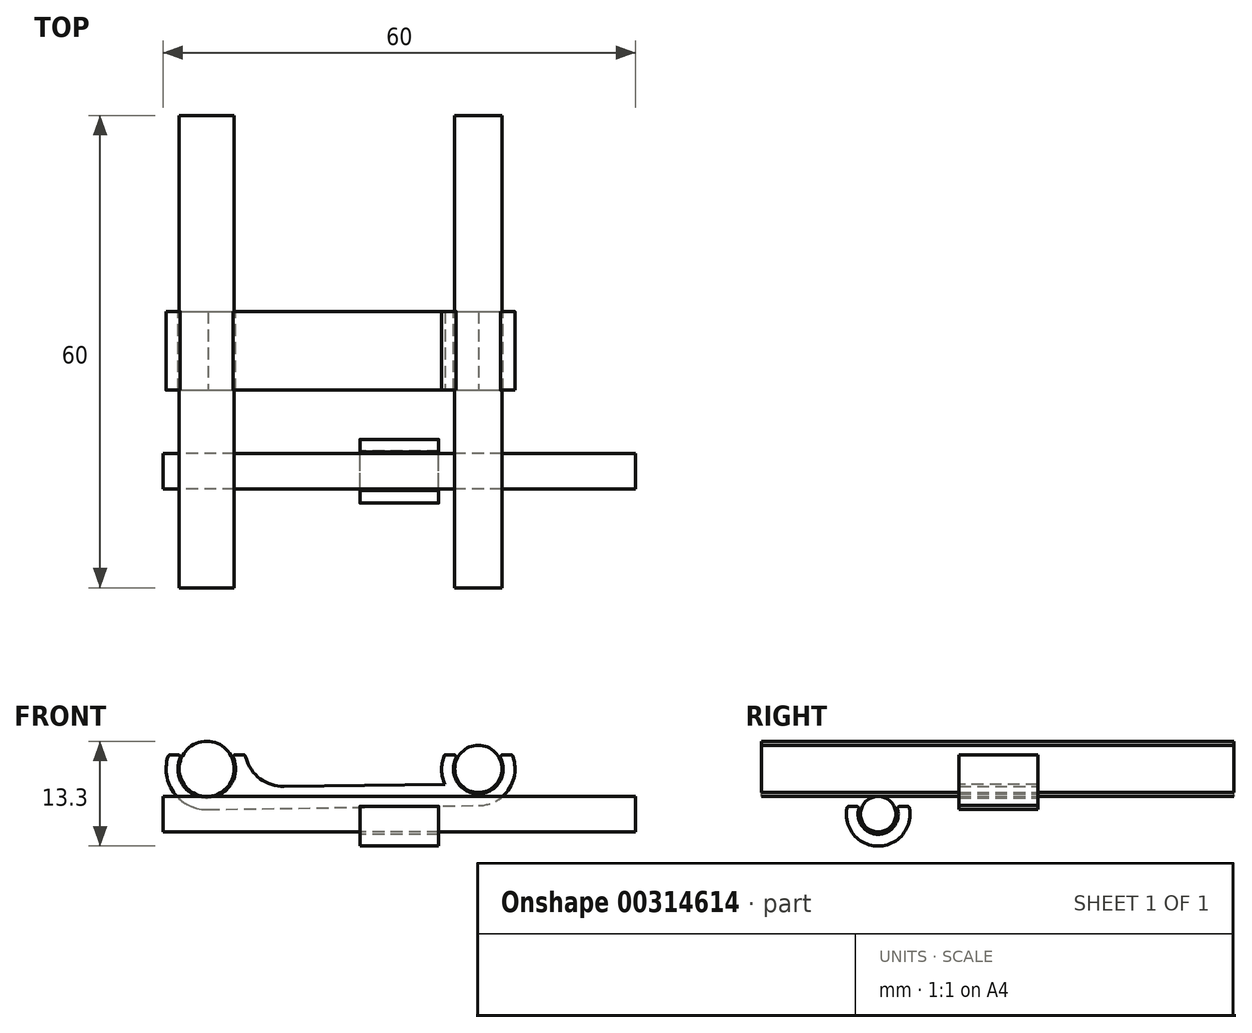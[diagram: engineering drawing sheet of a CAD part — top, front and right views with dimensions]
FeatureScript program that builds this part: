
annotation { "Feature Type Name" : "Feature", "Feature Type Description" : "" }
export const myFeature = defineFeature(function(context is Context, id is Id, definition is map)
    precondition{}
    {
        {
            var Q0;
            Q0=qCreatedBy(makeId("Front.planeOp"),FACE);
            var sketch = newSketch(context, id + "F0", { "sketchPlane" : qUnion([Q0])});
            skCircle(sketch, "E0", {"center": v(-24.47, 18.65) * mm, "radius": 3.5 * mm});
            skCircle(sketch, "E1", {"center": v(10.03, 18.65) * mm, "radius": 3 * mm});
            skLineSegment(sketch, "E2", {"start": v(-27.97, 18.65) * mm, "end": v(13.03, 18.65) * mm, "construction": true});
            skPoint(sketch, "E3", {"position": v(0, 18.65) * mm});
            skLineSegment(sketch, "E4", {"start": v(0, 0) * mm, "end": v(0, 43.05) * mm, "construction": true});
            skSolve(sketch);
        }
        {
            var Q0;
            Q0 = qSketchRegion(id + "F0", true);
            extrude(context, id + "F1", {"entities" : qUnion([Q0]), "depth" : 60 * mm});
        }
        {
            var Q0;
            Q0=qCreatedBy(makeId("Right.planeOp"),FACE);
            var sketch = newSketch(context, id + "F2", { "sketchPlane" : qUnion([Q0])});
            skCircle(sketch, "E5", {"center": v(-45.18, 12.9) * mm, "radius": 2.25 * mm});
            skLineSegment(sketch, "E6.0", {"start": v(-60, 15.15) * mm, "end": v(-60, 22.15) * mm, "construction": true});
            skLineSegment(sketch, "E7", {"start": v(-60, 15.15) * mm, "end": v(7.17, 15.15) * mm, "construction": true});
            skSolve(sketch);
        }
        {
            var Q0;
            Q0 = qSketchRegion(id + "F2", true);
            extrude(context, id + "F3", {"entities" : qUnion([Q0]), "endBound" : BoundingType.SYMMETRIC, "depth" : 60 * mm});
        }
        {
            var Q0;
            Q0=qCreatedBy(makeId("Right.planeOp"),FACE);
            var sketch = newSketch(context, id + "F4", { "sketchPlane" : qUnion([Q0])});
            skCircle(sketch, "E8.0", {"center": v(-45.18, 12.9) * mm, "radius": 2.25 * mm, "construction": true});
            skLineSegment(sketch, "E9", {"start": v(-45.18, 12.9) * mm, "end": v(-45.18, 13.9) * mm, "construction": true});
            skLineSegment(sketch, "E10", {"start": v(-41.25, 13.9) * mm, "end": v(-41.25, 13.9) * mm});
            skLineSegment(sketch, "E11", {"start": v(-47.52, 13.9) * mm, "end": v(-49.1, 13.9) * mm});
            skLineSegment(sketch, "E12", {"start": v(-42.83, 13.9) * mm, "end": v(-47.52, 13.9) * mm, "construction": true});
            skArc(sketch, "E13", {"start": v(-47.52, 13.9) * mm, "mid": v(-45.18, 10.35) * mm, "end": v(-42.83, 13.9) * mm});
            skArc(sketch, "E14", {"start": v(-42.83, 13.9) * mm, "mid": v(-45.18, 15.45) * mm, "end": v(-47.52, 13.9) * mm, "construction": true});
            skArc(sketch, "E15", {"start": v(-49.1, 13.9) * mm, "mid": v(-45.18, 8.85) * mm, "end": v(-41.25, 13.9) * mm});
            skArc(sketch, "E16", {"start": v(-41.25, 13.9) * mm, "mid": v(-45.18, 16.95) * mm, "end": v(-49.1, 13.9) * mm, "construction": true});
            skLineSegment(sketch, "E17", {"start": v(-41.25, 13.9) * mm, "end": v(-42.83, 13.9) * mm});
            skSolve(sketch);
        }
        {
            var Q0;
            Q0=makeQuery(id+"F4.imprint","IMPRINT",FACE,{"disambiguationData":[TD([[makeQuery(id+"F4.imprint","IMPRINT",EDGE,{"derivedFrom":sQuery(id+"F4.wireOp",EDGE,"E11")}),1.0]])]});
            extrude(context, id + "F5", {"entities" : qUnion([Q0]), "endBound" : BoundingType.SYMMETRIC, "depth" : 10 * mm});
        }
        {
            var Q0;
            Q0=makeQuery(id+"F5.opExtrude","SWEPT_EDGE",EDGE,{"disambiguationData":[OSD([sQuery(id+"F4.wireOp",EDGE,"E15"),sQuery(id+"F4.wireOp",EDGE,"E17")])]});
            var Q1;
            Q1=makeQuery(id+"F5.opExtrude","SWEPT_EDGE",EDGE,{"disambiguationData":[OSD([sQuery(id+"F4.wireOp",EDGE,"E13"),sQuery(id+"F4.wireOp",EDGE,"E17")])]});
            var Q2;
            Q2=makeQuery(id+"F5.opExtrude","SWEPT_EDGE",EDGE,{"disambiguationData":[OSD([sQuery(id+"F4.wireOp",EDGE,"E11"),sQuery(id+"F4.wireOp",EDGE,"E13")])]});
            var Q3;
            Q3=makeQuery(id+"F5.opExtrude","SWEPT_EDGE",EDGE,{"disambiguationData":[OSD([sQuery(id+"F4.wireOp",EDGE,"E11"),sQuery(id+"F4.wireOp",EDGE,"E15")])]});
            fillet(context, id + "F6", {"entities" : qUnion([Q0, Q1, Q2, Q3]), "radius" : 0.3 * mm, "tangentPropagation" : true, "allowEdgeOverflow" : false});
        }
        {
            var Q0;
            Q0=qCreatedBy(makeId("Front.planeOp"),FACE);
            cPlane(context, id + "F7", {"entities" : qUnion([Q0]), "cplaneType" : CPlaneType.OFFSET, "offset" : 29.9 * mm, "width" : 150 * mm, "height" : 150 * mm});
        }
        {
            var Q0;
            Q0=qCreatedBy(id+"F7.planeOp",FACE);
            var sketch = newSketch(context, id + "F8", { "sketchPlane" : qUnion([Q0])});
            skCircle(sketch, "E18.0", {"center": v(-24.47, 18.65) * mm, "radius": 3.5 * mm, "construction": true});
            skLineSegment(sketch, "E19", {"start": v(-26.27, 26.23) * mm, "end": v(-26.27, 23.48) * mm, "construction": true});
            skLineSegment(sketch, "E20", {"start": v(-26.27, 23.48) * mm, "end": v(-26.27, 21.83) * mm});
            skLineSegment(sketch, "E21", {"start": v(-26.27, 15.46) * mm, "end": v(-26.27, 13.8) * mm});
            skLineSegment(sketch, "E22", {"start": v(-26.27, 13.8) * mm, "end": v(-26.27, 11.64) * mm, "construction": true});
            skArc(sketch, "E23", {"start": v(-26.27, 21.83) * mm, "mid": v(-28.13, 18.65) * mm, "end": v(-26.27, 15.46) * mm, "construction": true});
            skArc(sketch, "E24", {"start": v(-26.27, 15.46) * mm, "mid": v(-20.8, 18.65) * mm, "end": v(-26.27, 21.83) * mm});
            skArc(sketch, "E25", {"start": v(-26.27, 13.8) * mm, "mid": v(-19.3, 18.65) * mm, "end": v(-26.27, 23.48) * mm});
            skArc(sketch, "E26", {"start": v(-26.27, 23.48) * mm, "mid": v(-29.63, 18.65) * mm, "end": v(-26.27, 13.8) * mm, "construction": true});
            skLineSegment(sketch, "E27", {"start": v(-26.27, 21.83) * mm, "end": v(-26.27, 15.46) * mm, "construction": true});
            skCircle(sketch, "E28.0", {"center": v(10.03, 18.65) * mm, "radius": 3 * mm, "construction": true});
            skLineSegment(sketch, "E29", {"start": v(11.83, 24.74) * mm, "end": v(11.83, 22.94) * mm, "construction": true});
            skArc(sketch, "E30", {"start": v(11.83, 22.94) * mm, "mid": v(5.37, 18.65) * mm, "end": v(11.83, 14.35) * mm});
            skArc(sketch, "E31", {"start": v(11.83, 14.35) * mm, "mid": v(14.7, 18.65) * mm, "end": v(11.83, 22.94) * mm, "construction": true});
            skLineSegment(sketch, "E32", {"start": v(11.83, 16.05) * mm, "end": v(11.83, 14.35) * mm});
            skArc(sketch, "E33", {"start": v(11.83, 16.05) * mm, "mid": v(13.2, 18.65) * mm, "end": v(11.83, 21.24) * mm, "construction": true});
            skArc(sketch, "E34", {"start": v(11.83, 21.24) * mm, "mid": v(6.87, 18.65) * mm, "end": v(11.83, 16.05) * mm});
            skLineSegment(sketch, "E35", {"start": v(11.83, 21.24) * mm, "end": v(11.83, 16.05) * mm, "construction": true});
            skLineSegment(sketch, "E36", {"start": v(11.83, 22.94) * mm, "end": v(11.83, 21.24) * mm});
            skLineSegment(sketch, "E37", {"start": v(11.83, 14.35) * mm, "end": v(11.83, 11.12) * mm, "construction": true});
            skSolve(sketch);
        }
        {
            var Q0;
            Q0=makeQuery(id+"F8.imprint","IMPRINT",FACE,{"disambiguationData":[TD([[makeQuery(id+"F8.imprint","IMPRINT",EDGE,{"derivedFrom":sQuery(id+"F8.wireOp",EDGE,"E20")}),1.0]])]});
            var Q1;
            Q1=makeQuery(id+"F8.imprint","IMPRINT",FACE,{"disambiguationData":[TD([[makeQuery(id+"F8.imprint","IMPRINT",EDGE,{"derivedFrom":sQuery(id+"F8.wireOp",EDGE,"E30")}),1.0]])]});
            extrude(context, id + "F9", {"entities" : qUnion([Q0, Q1]), "endBound" : BoundingType.SYMMETRIC, "depth" : 10 * mm});
        }
        {
            var Q0;
            Q0=makeQuery(id+"F9.opExtrude","SWEPT_BODY",BODY,{"disambiguationData":[OSD([sQuery(id+"F8.wireOp",EDGE,"E20"),sQuery(id+"F8.wireOp",EDGE,"E21"),sQuery(id+"F8.wireOp",EDGE,"E24"),sQuery(id+"F8.wireOp",EDGE,"E25")])]});
            var Q1;
            Q1=makeQuery(id+"F1.opExtrude","SWEPT_FACE",FACE,{"disambiguationData":[OSD([sQuery(id+"F0.wireOp",EDGE,"E0")])]});
            transform(context, id + "F10", {"entities" : qUnion([Q0]), "transformType" : TransformType.ROTATION, "transformAxis" : qUnion([Q1]), "angle" : 90 * degree, "makeCopy" : false});
        }
        {
            var Q0;
            Q0=makeQuery(id+"F9.opExtrude","SWEPT_BODY",BODY,{"disambiguationData":[OSD([sQuery(id+"F8.wireOp",EDGE,"E30"),sQuery(id+"F8.wireOp",EDGE,"E32"),sQuery(id+"F8.wireOp",EDGE,"E34"),sQuery(id+"F8.wireOp",EDGE,"E36")])]});
            var Q1;
            Q1=makeQuery(id+"F9.opExtrude","CAP_EDGE",EDGE,{"disambiguationData":[OSD([sQuery(id+"F8.wireOp",EDGE,"E32")])],"isStart":true});
            var Q2;
            Q2=makeQuery(id+"F9.opExtrude","CAP_VERTEX",VERTEX,{"disambiguationData":[OSD([sQuery(id+"F8.wireOp",EDGE,"E30"),sQuery(id+"F8.wireOp",EDGE,"E32")])],"isStart":true});
            var Q3;
            Q3=makeQuery(id+"F1.opExtrude","SWEPT_FACE",FACE,{"disambiguationData":[OSD([sQuery(id+"F0.wireOp",EDGE,"E1")])]});
            transform(context, id + "F11", {"entities" : qUnion([Q0]), "transformType" : TransformType.ROTATION, "transformAxis" : qUnion([Q3]), "angle" : 270 * degree, "makeCopy" : false});
        }
        {
            var Q0;
            Q0=makeQuery(id+"F9.opExtrude","CAP_FACE",FACE,{"disambiguationData":[OSD([sQuery(id+"F8.wireOp",EDGE,"E20"),sQuery(id+"F8.wireOp",EDGE,"E21"),sQuery(id+"F8.wireOp",EDGE,"E24"),sQuery(id+"F8.wireOp",EDGE,"E25")])],"isStart":false});
            var sketch = newSketch(context, id + "F12", { "sketchPlane" : qUnion([Q0])});
            skLineSegment(sketch, "E38.1.0", {"start": v(7.44, 20.45) * mm, "end": v(5.73, 20.45) * mm});
            skArc(sketch, "E38.1.1", {"start": v(5.73, 20.45) * mm, "mid": v(10.03, 13.99) * mm, "end": v(14.33, 20.45) * mm});
            skLineSegment(sketch, "E38.1.2", {"start": v(14.33, 20.45) * mm, "end": v(12.63, 20.45) * mm});
            skArc(sketch, "E38.1.3", {"start": v(12.63, 20.45) * mm, "mid": v(10.03, 15.49) * mm, "end": v(7.44, 20.45) * mm});
            skArc(sketch, "E39.0", {"start": v(-29.3, 20.45) * mm, "mid": v(-24.47, 13.49) * mm, "end": v(-19.63, 20.45) * mm});
            skLineSegment(sketch, "E40", {"start": v(-24.47, 13.49) * mm, "end": v(10.03, 13.99) * mm});
            skLineSegment(sketch, "E41", {"start": v(-19.86, 16.33) * mm, "end": v(5.8, 16.7) * mm});
            skSolve(sketch);
        }
        {
            var Q0;
            {var subQ3=sQuery(id+"F12.wireOp",EDGE,"E41");Q0=makeQuery(id+"F12.imprint","IMPRINT",FACE,{"disambiguationData":[TD([[makeQuery(id+"F12.imprint","IMPRINT",EDGE,{"derivedFrom":subQ3}),-1.0]])]});}
            extrude(context, id + "F13", {"entities" : qUnion([Q0]), "operationType" : NewBodyOperationType.ADD, "oppositeDirection" : true, "depth" : 10 * mm});
        }
        {
            var Q0;
            Q0=makeQuery(id+"F9.opExtrude","SWEPT_EDGE",EDGE,{"disambiguationData":[OSD([sQuery(id+"F8.wireOp",EDGE,"E20"),sQuery(id+"F8.wireOp",EDGE,"E25")])]});
            var Q1;
            Q1=makeQuery(id+"F9.opExtrude","SWEPT_EDGE",EDGE,{"disambiguationData":[OSD([sQuery(id+"F8.wireOp",EDGE,"E20"),sQuery(id+"F8.wireOp",EDGE,"E24")])]});
            var Q2;
            Q2=makeQuery(id+"F9.opExtrude","SWEPT_EDGE",EDGE,{"disambiguationData":[OSD([sQuery(id+"F8.wireOp",EDGE,"E21"),sQuery(id+"F8.wireOp",EDGE,"E24")])]});
            var Q3;
            Q3=makeQuery(id+"F9.opExtrude","SWEPT_EDGE",EDGE,{"disambiguationData":[OSD([sQuery(id+"F8.wireOp",EDGE,"E21"),sQuery(id+"F8.wireOp",EDGE,"E25")])]});
            var Q4;
            Q4=makeQuery(id+"F9.opExtrude","SWEPT_EDGE",EDGE,{"disambiguationData":[OSD([sQuery(id+"F8.wireOp",EDGE,"E34"),sQuery(id+"F8.wireOp",EDGE,"E36")])]});
            var Q5;
            Q5=makeQuery(id+"F9.opExtrude","SWEPT_EDGE",EDGE,{"disambiguationData":[OSD([sQuery(id+"F8.wireOp",EDGE,"E30"),sQuery(id+"F8.wireOp",EDGE,"E36")])]});
            var Q6;
            Q6=makeQuery(id+"F9.opExtrude","SWEPT_EDGE",EDGE,{"disambiguationData":[OSD([sQuery(id+"F8.wireOp",EDGE,"E30"),sQuery(id+"F8.wireOp",EDGE,"E32")])]});
            var Q7;
            Q7=makeQuery(id+"F9.opExtrude","SWEPT_EDGE",EDGE,{"disambiguationData":[OSD([sQuery(id+"F8.wireOp",EDGE,"E32"),sQuery(id+"F8.wireOp",EDGE,"E34")])]});
            fillet(context, id + "F14", {"entities" : qUnion([Q0, Q1, Q2, Q3, Q4, Q5, Q6, Q7]), "radius" : 0.3 * mm, "tangentPropagation" : true, "allowEdgeOverflow" : false});
        }
        {
            var Q0;
            Q0=makeQuery(id+"F13.opExtrude","SWEPT_EDGE",EDGE,{"disambiguationData":[OSD([sQuery(id+"F12.wireOp",EDGE,"E39.0"),sQuery(id+"F12.wireOp",EDGE,"E41")])]});
            var Q1;
            Q1=makeQuery(id+"F13.opExtrude","SWEPT_EDGE",EDGE,{"disambiguationData":[OSD([sQuery(id+"F12.wireOp",EDGE,"E38.1.1"),sQuery(id+"F12.wireOp",EDGE,"E41")])]});
            fillet(context, id + "F15", {"entities" : qUnion([Q0, Q1]), "radius" : 5 * mm, "tangentPropagation" : true, "allowEdgeOverflow" : false});
        }
    });
